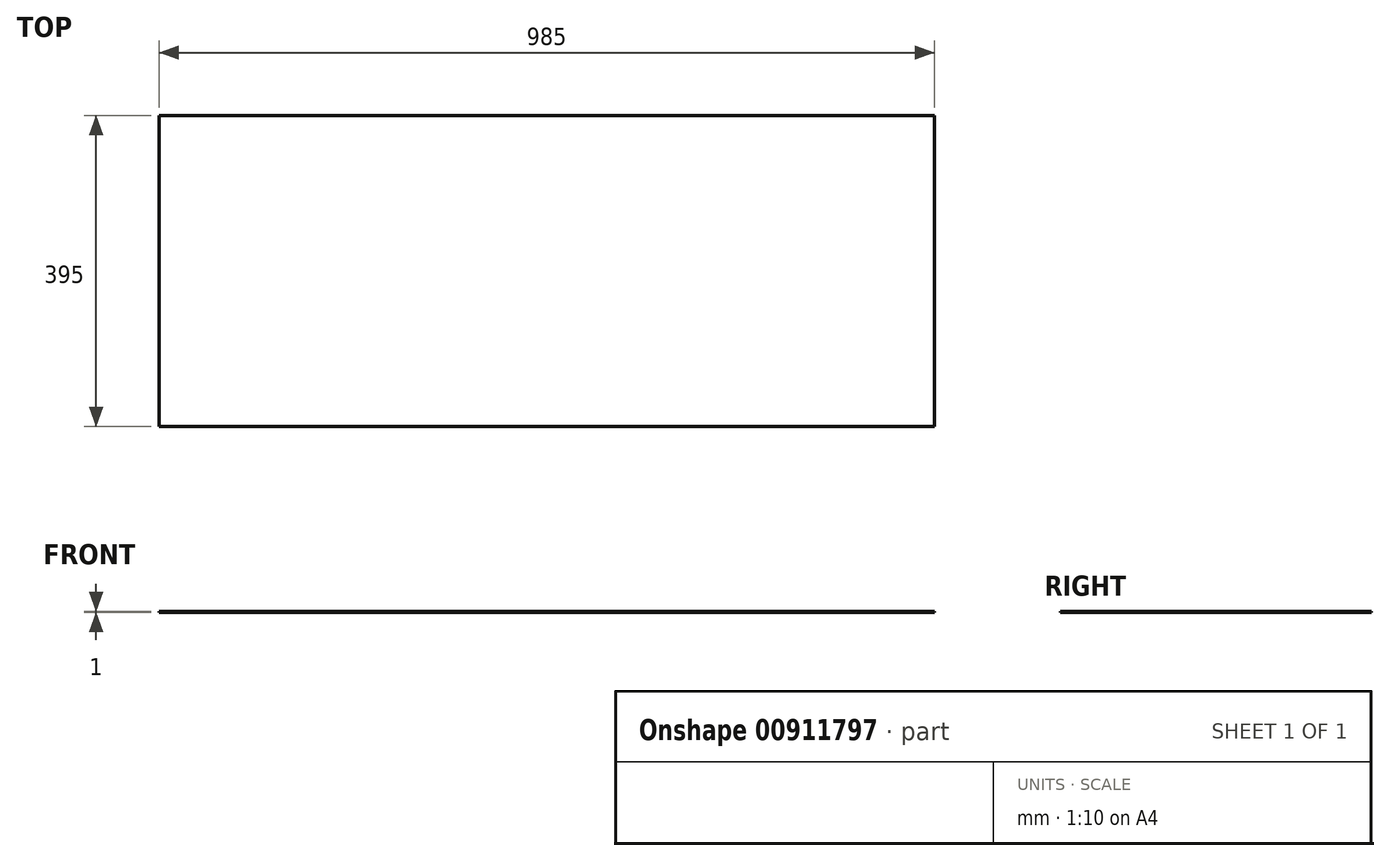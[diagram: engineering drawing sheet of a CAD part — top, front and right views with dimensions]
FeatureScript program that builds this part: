
annotation { "Feature Type Name" : "Feature", "Feature Type Description" : "" }
export const myFeature = defineFeature(function(context is Context, id is Id, definition is map)
    precondition{}
    {
        {
            var Q0;
            Q0=qCreatedBy(makeId("Top.planeOp"),FACE);
            var sketch = newSketch(context, id + "F0", { "sketchPlane" : qUnion([Q0])});
            skLineSegment(sketch, "E0.bottom", {"start": v(-492.5, 197.5) * mm, "end": v(492.5, 197.5) * mm});
            skLineSegment(sketch, "E0.top", {"start": v(-492.5, -197.5) * mm, "end": v(492.5, -197.5) * mm});
            skLineSegment(sketch, "E0.left", {"start": v(-492.5, 197.5) * mm, "end": v(-492.5, -197.5) * mm});
            skLineSegment(sketch, "E0.right", {"start": v(492.5, 197.5) * mm, "end": v(492.5, -197.5) * mm});
            skPoint(sketch, "E0.middle", {"position": v(0, 0) * mm});
            skSolve(sketch);
        }
        {
            var Q0;
            Q0=qSketchRegion(id+"F0",true);
            extrude(context, id + "F1", {"entities" : qUnion([Q0]), "depth" : 1 * mm, "offsetDistance" : 25 * mm});
        }
    });
